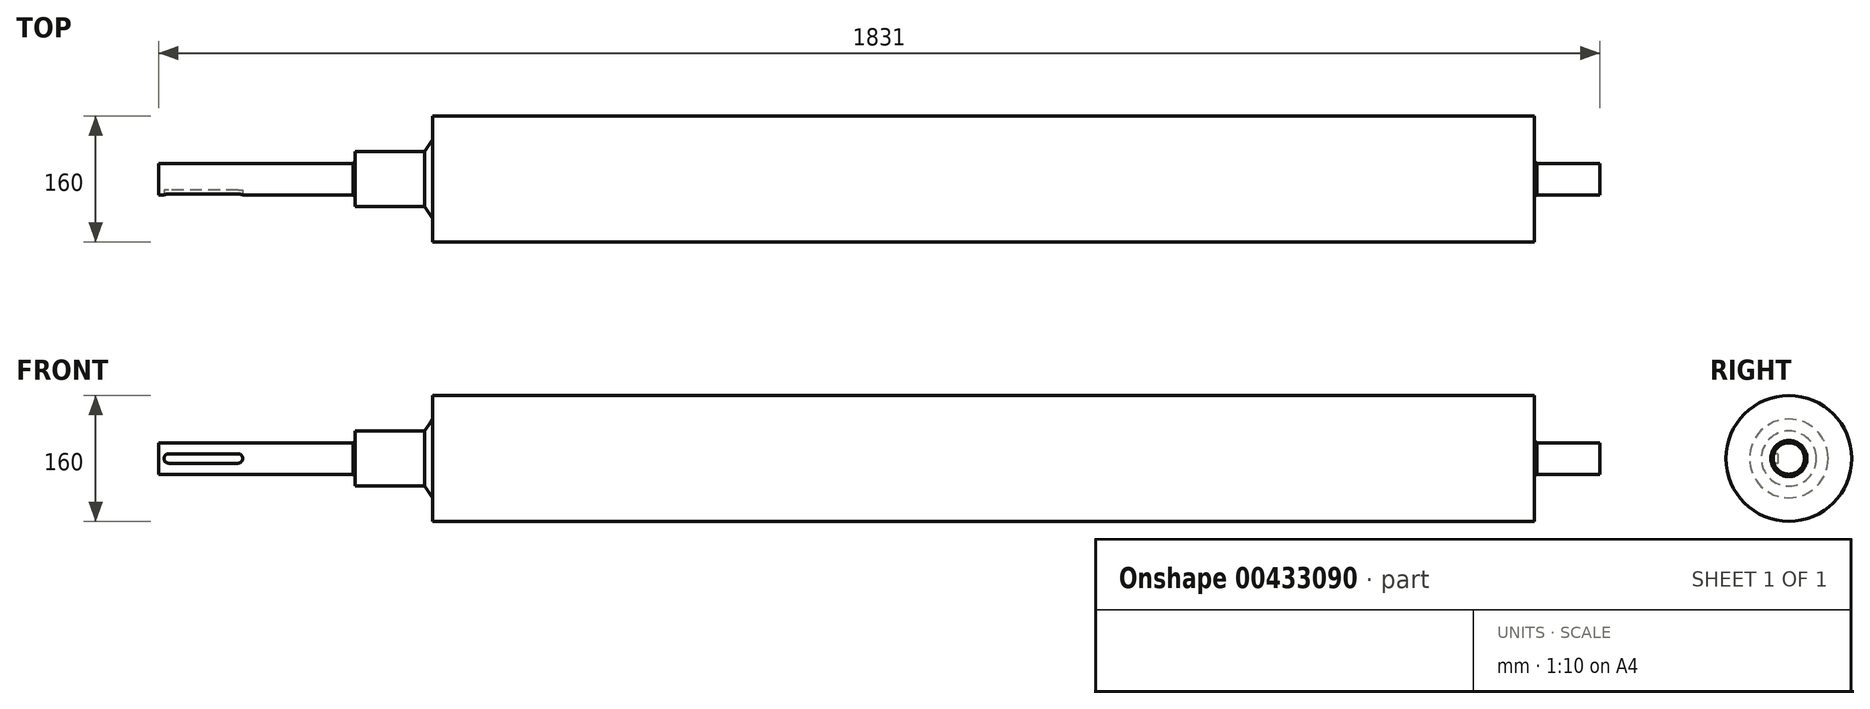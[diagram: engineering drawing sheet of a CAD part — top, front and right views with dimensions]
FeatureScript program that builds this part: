
annotation { "Feature Type Name" : "Feature", "Feature Type Description" : "" }
export const myFeature = defineFeature(function(context is Context, id is Id, definition is map)
    precondition{}
    {
        {
            var Q0;
            Q0=qCreatedBy(makeId("Front.planeOp"),FACE);
            var sketch = newSketch(context, id + "F0", { "sketchPlane" : qUnion([Q0])});
            skLineSegment(sketch, "E0", {"start": v(0, 0) * mm, "end": v(783, 0) * mm});
            skLineSegment(sketch, "E1", {"start": v(783, 0) * mm, "end": v(783, 20) * mm});
            skLineSegment(sketch, "E2", {"start": v(783, 20) * mm, "end": v(700, 20) * mm});
            skLineSegment(sketch, "E3", {"start": v(700, 20) * mm, "end": v(700, 80) * mm});
            skLineSegment(sketch, "E4", {"start": v(700, 80) * mm, "end": v(-700, 80) * mm});
            skLineSegment(sketch, "E5", {"start": v(-700, 80) * mm, "end": v(-700, 35) * mm});
            skLineSegment(sketch, "E6", {"start": v(-700, 35) * mm, "end": v(-798, 35) * mm});
            skLineSegment(sketch, "E7", {"start": v(-798, 35) * mm, "end": v(-798, 20) * mm});
            skLineSegment(sketch, "E8", {"start": v(-798, 20) * mm, "end": v(-1048, 20) * mm});
            skLineSegment(sketch, "E9", {"start": v(-1048, 20) * mm, "end": v(-1048, 0) * mm});
            skLineSegment(sketch, "E10", {"start": v(-1048, 0) * mm, "end": v(0, 0) * mm});
            skPoint(sketch, "E11.end.orphan", {"position": v(-700, 50) * mm});
            skPoint(sketch, "E11.start.orphan", {"position": v(-710, 35) * mm});
            skPoint(sketch, "E12.end.orphan", {"position": v(-798, 23) * mm});
            skPoint(sketch, "E12.start.orphan", {"position": v(-801, 20) * mm});
            skPoint(sketch, "E13.end.orphan", {"position": v(703, 20) * mm});
            skPoint(sketch, "E13.start.orphan", {"position": v(700, 23) * mm});
            skLineSegment(sketch, "E14", {"start": v(-801, 20) * mm, "end": v(-798, 23) * mm});
            skLineSegment(sketch, "E15", {"start": v(-710, 35) * mm, "end": v(-700, 50) * mm});
            skLineSegment(sketch, "E16", {"start": v(700, 23) * mm, "end": v(703, 20) * mm});
            skSolve(sketch);
        }
        {
            var Q0;
            Q0 = qSketchRegion(id + "F0", true);
            var Q1;
            Q1=sQuery(id+"F0.wireOp",EDGE,"E0");
            revolve(context, id + "F1", {"entities" : qUnion([Q0]), "axis" : qUnion([Q1]), "revolveType" : RevolveType.FULL});
        }
        {
            var Q0;
            Q0=qCreatedBy(makeId("Front.planeOp"),FACE);
            cPlane(context, id + "F2", {"entities" : qUnion([Q0]), "cplaneType" : CPlaneType.OFFSET, "offset" : 20 * mm, "width" : 150 * mm, "height" : 150 * mm});
        }
        {
            var Q0;
            Q0=qCreatedBy(id+"F2.planeOp",FACE);
            var sketch = newSketch(context, id + "F3", { "sketchPlane" : qUnion([Q0])});
            skLineSegment(sketch, "E17.bottom", {"start": v(-947, 6) * mm, "end": v(-1035, 6) * mm});
            skLineSegment(sketch, "E17.top", {"start": v(-947, -6) * mm, "end": v(-1035, -6) * mm});
            skLineSegment(sketch, "E17.left", {"start": v(-941, 0) * mm, "end": v(-941, 0) * mm});
            skLineSegment(sketch, "E17.right", {"start": v(-1041, 0) * mm, "end": v(-1041, 0) * mm});
            skPoint(sketch, "E17.middle", {"position": v(-991, 0) * mm});
            skPoint(sketch, "E18.visualSharp", {"position": v(-1041, 6) * mm});
            skArc(sketch, "E18.filletArc", {"start": v(-1035, 6) * mm, "mid": v(-1039.24, 4.24) * mm, "end": v(-1041, 0) * mm});
            skPoint(sketch, "E19.visualSharp", {"position": v(-1041, -6) * mm});
            skArc(sketch, "E19.filletArc", {"start": v(-1041, 0) * mm, "mid": v(-1039.24, -4.24) * mm, "end": v(-1035, -6) * mm});
            skPoint(sketch, "E20.visualSharp", {"position": v(-941, -6) * mm});
            skArc(sketch, "E20.filletArc", {"start": v(-947, -6) * mm, "mid": v(-942.76, -4.24) * mm, "end": v(-941, 0) * mm});
            skPoint(sketch, "E21.visualSharp", {"position": v(-941, 6) * mm});
            skArc(sketch, "E21.filletArc", {"start": v(-941, 0) * mm, "mid": v(-942.76, 4.24) * mm, "end": v(-947, 6) * mm});
            skSolve(sketch);
        }
        {
            var Q0;
            Q0 = qSketchRegion(id + "F3", true);
            extrude(context, id + "F4", {"entities" : qUnion([Q0]), "operationType" : NewBodyOperationType.REMOVE, "oppositeDirection" : true, "depth" : 6 * mm});
        }
    });
